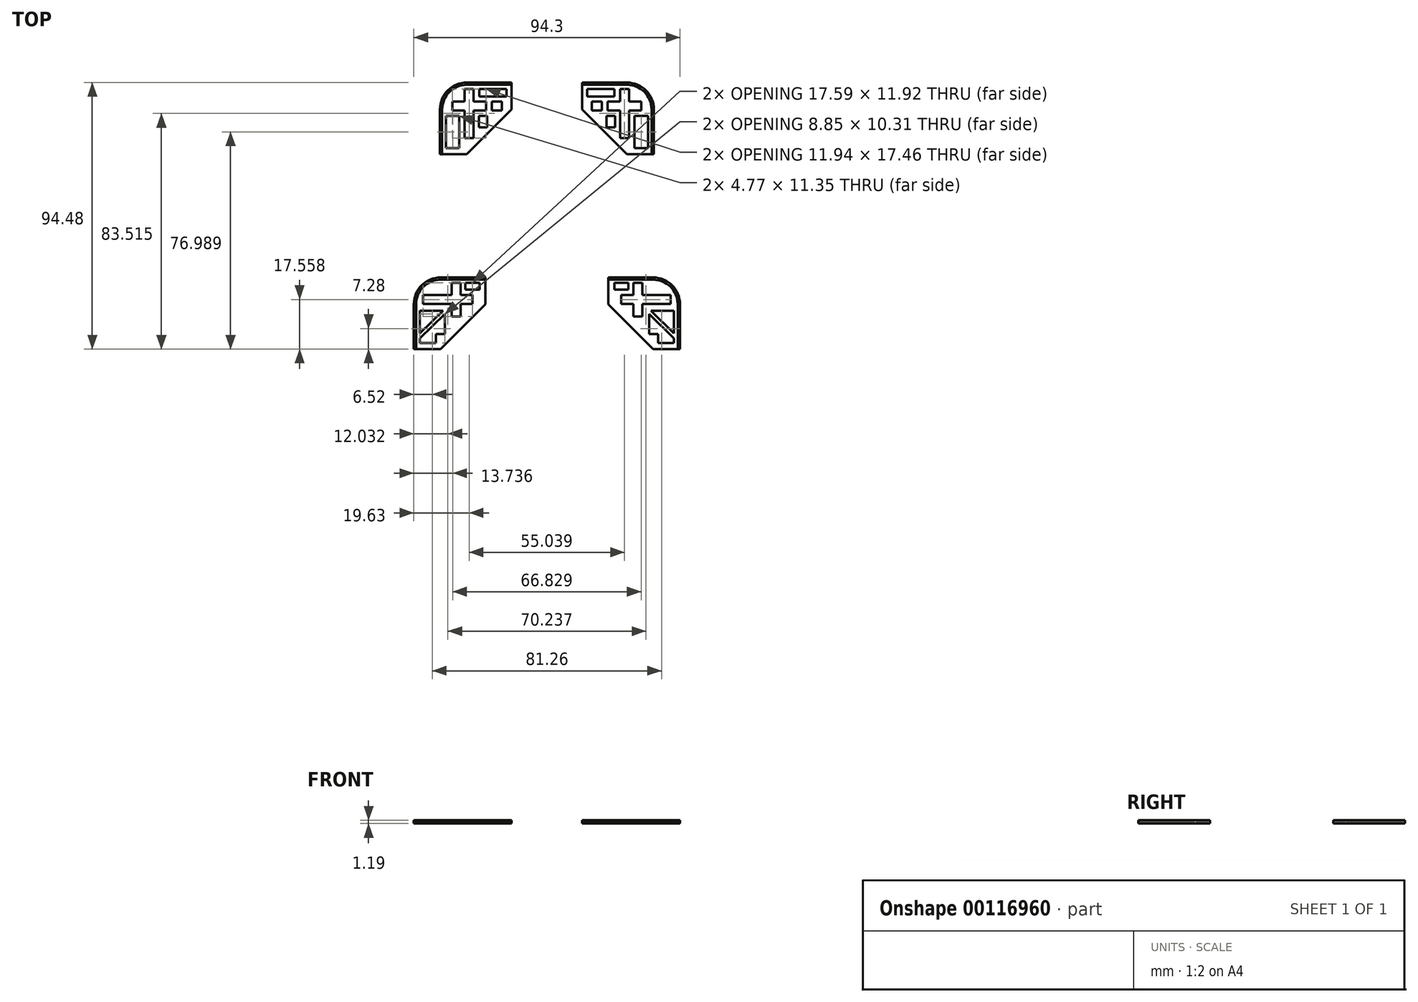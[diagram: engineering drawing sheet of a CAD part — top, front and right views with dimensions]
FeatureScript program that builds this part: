
annotation { "Feature Type Name" : "Feature", "Feature Type Description" : "" }
export const myFeature = defineFeature(function(context is Context, id is Id, definition is map)
    precondition{}
    {
        {
            var Q0;
            Q0=qCreatedBy(makeId("Top.planeOp"),FACE);
            var sketch = newSketch(context, id + "F0", { "sketchPlane" : qUnion([Q0])});
            skLineSegment(sketch, "E0", {"start": v(-37.9, 7.88) * mm, "end": v(-37.9, 23.75) * mm});
            skLineSegment(sketch, "E1", {"start": v(-37.9, 33.28) * mm, "end": v(-28.37, 33.28) * mm, "construction": true});
            skLineSegment(sketch, "E2", {"start": v(-37.9, 23.75) * mm, "end": v(-28.37, 23.75) * mm, "construction": true});
            skLineSegment(sketch, "E3", {"start": v(-28.37, 23.75) * mm, "end": v(-28.37, 33.28) * mm, "construction": true});
            skArc(sketch, "E4", {"start": v(-37.9, 23.75) * mm, "mid": v(-35.11, 30.49) * mm, "end": v(-28.37, 33.28) * mm});
            skLineSegment(sketch, "E5", {"start": v(-28.37, 33.28) * mm, "end": v(-12.5, 33.28) * mm});
            skLineSegment(sketch, "E6", {"start": v(-37.9, 23.75) * mm, "end": v(-37.9, 33.28) * mm, "construction": true});
            skLineSegment(sketch, "E7", {"start": v(-37.9, 7.88) * mm, "end": v(-28.37, 7.88) * mm});
            skLineSegment(sketch, "E8", {"start": v(-28.37, 7.88) * mm, "end": v(-12.5, 23.75) * mm});
            skLineSegment(sketch, "E9", {"start": v(-12.5, 23.75) * mm, "end": v(-12.5, 33.28) * mm});
            skLineSegment(sketch, "E10", {"start": v(-27.52, 35.55) * mm, "end": v(-27.52, 7.49) * mm, "construction": true});
            skLineSegment(sketch, "E11", {"start": v(-27.52, 31.05) * mm, "end": v(-29.1, 31.05) * mm});
            skLineSegment(sketch, "E12", {"start": v(-29.1, 31.05) * mm, "end": v(-29.1, 26.59) * mm});
            skLineSegment(sketch, "E13", {"start": v(-29.1, 26.59) * mm, "end": v(-33.5, 26.59) * mm});
            skLineSegment(sketch, "E14", {"start": v(-33.5, 26.59) * mm, "end": v(-33.5, 23.41) * mm});
            skLineSegment(sketch, "E15", {"start": v(-33.5, 23.41) * mm, "end": v(-29.1, 23.41) * mm});
            skLineSegment(sketch, "E16", {"start": v(-29.1, 23.41) * mm, "end": v(-29.1, 13.58) * mm});
            skLineSegment(sketch, "E17", {"start": v(-29.1, 13.58) * mm, "end": v(-27.52, 13.58) * mm});
            skLineSegment(sketch, "E18.MirrorCS", {"start": v(-27.52, 31.05) * mm, "end": v(-25.93, 31.05) * mm});
            skLineSegment(sketch, "E19.MirrorCS", {"start": v(-25.93, 31.05) * mm, "end": v(-25.93, 26.59) * mm});
            skLineSegment(sketch, "E20.MirrorCS", {"start": v(-25.93, 26.59) * mm, "end": v(-21.55, 26.59) * mm});
            skLineSegment(sketch, "E21.MirrorCS", {"start": v(-21.55, 26.59) * mm, "end": v(-21.55, 23.41) * mm});
            skLineSegment(sketch, "E22.MirrorCS", {"start": v(-21.55, 23.41) * mm, "end": v(-25.93, 23.41) * mm});
            skLineSegment(sketch, "E23.MirrorCS", {"start": v(-25.93, 23.41) * mm, "end": v(-25.93, 13.58) * mm});
            skLineSegment(sketch, "E24.MirrorCS", {"start": v(-25.93, 13.58) * mm, "end": v(-27.52, 13.58) * mm});
            skLineSegment(sketch, "E25.bottom", {"start": v(-23.9, 31.05) * mm, "end": v(-14.32, 31.05) * mm});
            skLineSegment(sketch, "E25.top", {"start": v(-23.9, 28.4) * mm, "end": v(-14.32, 28.4) * mm});
            skLineSegment(sketch, "E25.left", {"start": v(-23.9, 31.05) * mm, "end": v(-23.9, 28.4) * mm});
            skLineSegment(sketch, "E25.right", {"start": v(-14.32, 31.05) * mm, "end": v(-14.32, 28.4) * mm});
            skLineSegment(sketch, "E26.bottom", {"start": v(-24.13, 21.47) * mm, "end": v(-21.1, 21.47) * mm});
            skLineSegment(sketch, "E26.top", {"start": v(-24.13, 17.44) * mm, "end": v(-21.1, 17.44) * mm});
            skLineSegment(sketch, "E26.left", {"start": v(-24.13, 21.47) * mm, "end": v(-24.13, 17.44) * mm});
            skLineSegment(sketch, "E26.right", {"start": v(-21.1, 21.47) * mm, "end": v(-21.1, 17.44) * mm});
            skLineSegment(sketch, "E27.bottom", {"start": v(-31.03, 21.47) * mm, "end": v(-35.8, 21.47) * mm});
            skLineSegment(sketch, "E27.top", {"start": v(-31.03, 10.11) * mm, "end": v(-35.8, 10.11) * mm});
            skLineSegment(sketch, "E27.left", {"start": v(-31.03, 21.47) * mm, "end": v(-31.03, 10.11) * mm});
            skLineSegment(sketch, "E27.right", {"start": v(-35.8, 21.47) * mm, "end": v(-35.8, 10.11) * mm});
            skLineSegment(sketch, "E28.bottom", {"start": v(-19.47, 26.59) * mm, "end": v(-15.94, 26.59) * mm});
            skLineSegment(sketch, "E28.top", {"start": v(-19.47, 23.41) * mm, "end": v(-15.94, 23.41) * mm});
            skLineSegment(sketch, "E28.left", {"start": v(-19.47, 26.59) * mm, "end": v(-19.47, 23.41) * mm});
            skLineSegment(sketch, "E28.right", {"start": v(-15.94, 26.59) * mm, "end": v(-15.94, 23.41) * mm});
            skSolve(sketch);
        }
        {
            var Q0;
            Q0=makeQuery(id+"F0.imprint","IMPRINT",FACE,{"disambiguationData":[TD([[makeQuery(id+"F0.imprint","IMPRINT",EDGE,{"derivedFrom":sQuery(id+"F0.wireOp",EDGE,"E0")}),-1.0]])]});
            extrude(context, id + "F1", {"entities" : qUnion([Q0]), "depth" : 0.6 * mm});
        }
        {
            var Q0;
            Q0=makeQuery(id+"F1.opExtrude","SWEPT_BODY",BODY,{"disambiguationData":[OSD([sQuery(id+"F0.wireOp",EDGE,"E0"),sQuery(id+"F0.wireOp",EDGE,"E4"),sQuery(id+"F0.wireOp",EDGE,"E5"),sQuery(id+"F0.wireOp",EDGE,"E7"),sQuery(id+"F0.wireOp",EDGE,"E8"),sQuery(id+"F0.wireOp",EDGE,"E9"),sQuery(id+"F0.wireOp",EDGE,"E11"),sQuery(id+"F0.wireOp",EDGE,"E12"),sQuery(id+"F0.wireOp",EDGE,"E13"),sQuery(id+"F0.wireOp",EDGE,"E14"),sQuery(id+"F0.wireOp",EDGE,"E15"),sQuery(id+"F0.wireOp",EDGE,"E16"),sQuery(id+"F0.wireOp",EDGE,"E17"),sQuery(id+"F0.wireOp",EDGE,"E18.MirrorCS"),sQuery(id+"F0.wireOp",EDGE,"E19.MirrorCS"),sQuery(id+"F0.wireOp",EDGE,"E20.MirrorCS"),sQuery(id+"F0.wireOp",EDGE,"E21.MirrorCS"),sQuery(id+"F0.wireOp",EDGE,"E22.MirrorCS"),sQuery(id+"F0.wireOp",EDGE,"E23.MirrorCS"),sQuery(id+"F0.wireOp",EDGE,"E24.MirrorCS"),sQuery(id+"F0.wireOp",EDGE,"E25.bottom"),sQuery(id+"F0.wireOp",EDGE,"E25.top"),sQuery(id+"F0.wireOp",EDGE,"E25.left"),sQuery(id+"F0.wireOp",EDGE,"E25.right"),sQuery(id+"F0.wireOp",EDGE,"E26.bottom"),sQuery(id+"F0.wireOp",EDGE,"E26.top"),sQuery(id+"F0.wireOp",EDGE,"E26.left"),sQuery(id+"F0.wireOp",EDGE,"E26.right"),sQuery(id+"F0.wireOp",EDGE,"E27.bottom"),sQuery(id+"F0.wireOp",EDGE,"E27.top"),sQuery(id+"F0.wireOp",EDGE,"E27.left"),sQuery(id+"F0.wireOp",EDGE,"E27.right"),sQuery(id+"F0.wireOp",EDGE,"E28.bottom"),sQuery(id+"F0.wireOp",EDGE,"E28.top"),sQuery(id+"F0.wireOp",EDGE,"E28.left"),sQuery(id+"F0.wireOp",EDGE,"E28.right")])]});
            var Q1;
            Q1=qCreatedBy(makeId("Right.planeOp"),FACE);
            mirror(context, id + "F2", {"entities" : qUnion([Q0]), "mirrorPlane" : qUnion([Q1])});
        }
        {
            var Q0;
            Q0=qCreatedBy(makeId("Top.planeOp"),FACE);
            var sketch = newSketch(context, id + "F3", { "sketchPlane" : qUnion([Q0])});
            skLineSegment(sketch, "E29", {"start": v(-47.15, -61.2) * mm, "end": v(-47.15, -45.32) * mm});
            skLineSegment(sketch, "E30", {"start": v(-47.15, -35.8) * mm, "end": v(-37.63, -35.8) * mm, "construction": true});
            skLineSegment(sketch, "E31", {"start": v(-47.15, -45.32) * mm, "end": v(-37.63, -45.32) * mm, "construction": true});
            skLineSegment(sketch, "E32", {"start": v(-37.63, -45.32) * mm, "end": v(-37.63, -35.8) * mm, "construction": true});
            skArc(sketch, "E33", {"start": v(-47.15, -45.32) * mm, "mid": v(-44.36, -38.59) * mm, "end": v(-37.63, -35.8) * mm});
            skLineSegment(sketch, "E34", {"start": v(-37.63, -35.8) * mm, "end": v(-21.75, -35.8) * mm});
            skLineSegment(sketch, "E35", {"start": v(-47.15, -45.32) * mm, "end": v(-47.15, -35.8) * mm, "construction": true});
            skLineSegment(sketch, "E36", {"start": v(-47.15, -61.2) * mm, "end": v(-37.63, -61.2) * mm});
            skLineSegment(sketch, "E37", {"start": v(-37.63, -61.2) * mm, "end": v(-21.75, -45.32) * mm});
            skLineSegment(sketch, "E38", {"start": v(-21.75, -45.32) * mm, "end": v(-21.75, -35.8) * mm});
            skLineSegment(sketch, "E39.bottom", {"start": v(-36.85, -47.55) * mm, "end": v(-45.05, -47.55) * mm});
            skLineSegment(sketch, "E39.top", {"start": v(-36.2, -55.81) * mm, "end": v(-39.38, -55.81) * mm});
            skLineSegment(sketch, "E39.left", {"start": v(-36.2, -48.76) * mm, "end": v(-36.2, -55.81) * mm});
            skLineSegment(sketch, "E39.right", {"start": v(-45.05, -47.55) * mm, "end": v(-45.05, -55.57) * mm});
            skLineSegment(sketch, "E40", {"start": v(-26.32, -43.27) * mm, "end": v(-26.32, -42.05) * mm});
            skLineSegment(sketch, "E41", {"start": v(-26.32, -42.05) * mm, "end": v(-30.61, -42.05) * mm});
            skLineSegment(sketch, "E42", {"start": v(-30.61, -42.05) * mm, "end": v(-30.61, -37.68) * mm});
            skLineSegment(sketch, "E43", {"start": v(-30.61, -37.68) * mm, "end": v(-33.79, -37.68) * mm});
            skLineSegment(sketch, "E44", {"start": v(-33.79, -37.68) * mm, "end": v(-33.79, -42.05) * mm});
            skLineSegment(sketch, "E45", {"start": v(-33.79, -42.05) * mm, "end": v(-43.91, -42.05) * mm});
            skLineSegment(sketch, "E46", {"start": v(-43.91, -42.05) * mm, "end": v(-43.91, -45.23) * mm});
            skLineSegment(sketch, "E47", {"start": v(-43.91, -45.23) * mm, "end": v(-33.79, -45.23) * mm});
            skLineSegment(sketch, "E48", {"start": v(-33.79, -45.23) * mm, "end": v(-33.79, -49.6) * mm});
            skLineSegment(sketch, "E49", {"start": v(-33.79, -49.6) * mm, "end": v(-30.61, -49.6) * mm});
            skLineSegment(sketch, "E50", {"start": v(-30.61, -49.6) * mm, "end": v(-30.61, -45.23) * mm});
            skLineSegment(sketch, "E51", {"start": v(-30.61, -45.23) * mm, "end": v(-26.32, -45.23) * mm});
            skLineSegment(sketch, "E52", {"start": v(-26.32, -45.23) * mm, "end": v(-26.32, -43.27) * mm});
            skLineSegment(sketch, "E53.bottom", {"start": v(-28.87, -40.1) * mm, "end": v(-23.87, -40.1) * mm});
            skLineSegment(sketch, "E53.top", {"start": v(-28.87, -37.7) * mm, "end": v(-23.87, -37.7) * mm});
            skLineSegment(sketch, "E53.left", {"start": v(-28.87, -40.1) * mm, "end": v(-28.87, -37.7) * mm});
            skLineSegment(sketch, "E53.right", {"start": v(-23.87, -40.1) * mm, "end": v(-23.87, -37.7) * mm});
            skLineSegment(sketch, "E54.top", {"start": v(-45.05, -59.08) * mm, "end": v(-39.38, -59.08) * mm});
            skLineSegment(sketch, "E54.left", {"start": v(-45.05, -57.4) * mm, "end": v(-45.05, -59.08) * mm});
            skLineSegment(sketch, "E54.right", {"start": v(-39.38, -55.81) * mm, "end": v(-39.38, -59.08) * mm});
            skLineSegment(sketch, "E55", {"start": v(-36.85, -47.55) * mm, "end": v(-45.05, -55.57) * mm});
            skLineSegment(sketch, "E56", {"start": v(-36.2, -48.76) * mm, "end": v(-45.05, -57.4) * mm});
            skSolve(sketch);
        }
        {
            var Q0;
            Q0=makeQuery(id+"F3.imprint","IMPRINT",FACE,{"disambiguationData":[TD([[makeQuery(id+"F3.imprint","IMPRINT",EDGE,{"derivedFrom":sQuery(id+"F3.wireOp",EDGE,"E29")}),-1.0]])]});
            extrude(context, id + "F4", {"entities" : qUnion([Q0]), "depth" : 0.6 * mm});
        }
        {
            var Q0;
            Q0=makeQuery(id+"F4.opExtrude","SWEPT_BODY",BODY,{"disambiguationData":[OSD([sQuery(id+"F3.wireOp",EDGE,"E29"),sQuery(id+"F3.wireOp",EDGE,"E33"),sQuery(id+"F3.wireOp",EDGE,"E34"),sQuery(id+"F3.wireOp",EDGE,"E36"),sQuery(id+"F3.wireOp",EDGE,"E37"),sQuery(id+"F3.wireOp",EDGE,"E38"),sQuery(id+"F3.wireOp",EDGE,"E39.bottom"),sQuery(id+"F3.wireOp",EDGE,"E39.top"),sQuery(id+"F3.wireOp",EDGE,"E39.left"),sQuery(id+"F3.wireOp",EDGE,"E39.right"),sQuery(id+"F3.wireOp",EDGE,"E40"),sQuery(id+"F3.wireOp",EDGE,"E41"),sQuery(id+"F3.wireOp",EDGE,"E42"),sQuery(id+"F3.wireOp",EDGE,"E43"),sQuery(id+"F3.wireOp",EDGE,"E44"),sQuery(id+"F3.wireOp",EDGE,"E45"),sQuery(id+"F3.wireOp",EDGE,"E46"),sQuery(id+"F3.wireOp",EDGE,"E47"),sQuery(id+"F3.wireOp",EDGE,"E48"),sQuery(id+"F3.wireOp",EDGE,"E49"),sQuery(id+"F3.wireOp",EDGE,"E50"),sQuery(id+"F3.wireOp",EDGE,"E51"),sQuery(id+"F3.wireOp",EDGE,"E52"),sQuery(id+"F3.wireOp",EDGE,"E53.bottom"),sQuery(id+"F3.wireOp",EDGE,"E53.top"),sQuery(id+"F3.wireOp",EDGE,"E53.left"),sQuery(id+"F3.wireOp",EDGE,"E53.right"),sQuery(id+"F3.wireOp",EDGE,"E54.top"),sQuery(id+"F3.wireOp",EDGE,"E54.left"),sQuery(id+"F3.wireOp",EDGE,"E54.right"),sQuery(id+"F3.wireOp",EDGE,"E55"),sQuery(id+"F3.wireOp",EDGE,"E56")])]});
            var Q1;
            Q1=qCreatedBy(makeId("Right.planeOp"),FACE);
            mirror(context, id + "F5", {"entities" : qUnion([Q0]), "mirrorPlane" : qUnion([Q1])});
        }
        {
            var Q0;
            Q0=makeQuery(id+"F1.opExtrude","CAP_FACE",FACE,{"disambiguationData":[OSD([sQuery(id+"F0.wireOp",EDGE,"E0"),sQuery(id+"F0.wireOp",EDGE,"E4"),sQuery(id+"F0.wireOp",EDGE,"E5"),sQuery(id+"F0.wireOp",EDGE,"E7"),sQuery(id+"F0.wireOp",EDGE,"E8"),sQuery(id+"F0.wireOp",EDGE,"E9"),sQuery(id+"F0.wireOp",EDGE,"E11"),sQuery(id+"F0.wireOp",EDGE,"E12"),sQuery(id+"F0.wireOp",EDGE,"E13"),sQuery(id+"F0.wireOp",EDGE,"E14"),sQuery(id+"F0.wireOp",EDGE,"E15"),sQuery(id+"F0.wireOp",EDGE,"E16"),sQuery(id+"F0.wireOp",EDGE,"E17"),sQuery(id+"F0.wireOp",EDGE,"E18.MirrorCS"),sQuery(id+"F0.wireOp",EDGE,"E19.MirrorCS"),sQuery(id+"F0.wireOp",EDGE,"E20.MirrorCS"),sQuery(id+"F0.wireOp",EDGE,"E21.MirrorCS"),sQuery(id+"F0.wireOp",EDGE,"E22.MirrorCS"),sQuery(id+"F0.wireOp",EDGE,"E23.MirrorCS"),sQuery(id+"F0.wireOp",EDGE,"E24.MirrorCS"),sQuery(id+"F0.wireOp",EDGE,"E25.bottom"),sQuery(id+"F0.wireOp",EDGE,"E25.top"),sQuery(id+"F0.wireOp",EDGE,"E25.left"),sQuery(id+"F0.wireOp",EDGE,"E25.right"),sQuery(id+"F0.wireOp",EDGE,"E26.bottom"),sQuery(id+"F0.wireOp",EDGE,"E26.top"),sQuery(id+"F0.wireOp",EDGE,"E26.left"),sQuery(id+"F0.wireOp",EDGE,"E26.right"),sQuery(id+"F0.wireOp",EDGE,"E27.bottom"),sQuery(id+"F0.wireOp",EDGE,"E27.top"),sQuery(id+"F0.wireOp",EDGE,"E27.left"),sQuery(id+"F0.wireOp",EDGE,"E27.right"),sQuery(id+"F0.wireOp",EDGE,"E28.bottom"),sQuery(id+"F0.wireOp",EDGE,"E28.top"),sQuery(id+"F0.wireOp",EDGE,"E28.left"),sQuery(id+"F0.wireOp",EDGE,"E28.right")])],"isStart":false});
            var sketch = newSketch(context, id + "F6", { "sketchPlane" : qUnion([Q0])});
            skLineSegment(sketch, "E57.0", {"start": v(-28.37, 32.48) * mm, "end": v(-12.5, 32.48) * mm});
            skArc(sketch, "E57.1", {"start": v(-37.1, 23.75) * mm, "mid": v(-34.55, 29.93) * mm, "end": v(-28.37, 32.48) * mm});
            skLineSegment(sketch, "E57.2", {"start": v(-37.1, 7.88) * mm, "end": v(-37.1, 23.75) * mm});
            skArc(sketch, "E58.0", {"start": v(-37.9, 23.75) * mm, "mid": v(-35.11, 30.49) * mm, "end": v(-28.37, 33.28) * mm});
            skLineSegment(sketch, "E58.1", {"start": v(-28.37, 33.28) * mm, "end": v(-12.5, 33.28) * mm});
            skLineSegment(sketch, "E58.2", {"start": v(-37.9, 7.88) * mm, "end": v(-37.9, 23.75) * mm});
            skLineSegment(sketch, "E59", {"start": v(-12.5, 33.28) * mm, "end": v(-12.5, 32.48) * mm});
            skLineSegment(sketch, "E60", {"start": v(-37.9, 7.88) * mm, "end": v(-37.1, 7.88) * mm});
            skSolve(sketch);
        }
        {
            var Q0;
            Q0 = qSketchRegion(id + "F6", true);
            extrude(context, id + "F7", {"entities" : qUnion([Q0]), "operationType" : NewBodyOperationType.ADD, "depth" : 0.6 * mm});
        }
        {
            var Q0;
            Q0=makeQuery(id+"F1.opExtrude","SWEPT_BODY",BODY,{"disambiguationData":[OSD([sQuery(id+"F0.wireOp",EDGE,"E0"),sQuery(id+"F0.wireOp",EDGE,"E4"),sQuery(id+"F0.wireOp",EDGE,"E5"),sQuery(id+"F0.wireOp",EDGE,"E7"),sQuery(id+"F0.wireOp",EDGE,"E8"),sQuery(id+"F0.wireOp",EDGE,"E9"),sQuery(id+"F0.wireOp",EDGE,"E11"),sQuery(id+"F0.wireOp",EDGE,"E12"),sQuery(id+"F0.wireOp",EDGE,"E13"),sQuery(id+"F0.wireOp",EDGE,"E14"),sQuery(id+"F0.wireOp",EDGE,"E15"),sQuery(id+"F0.wireOp",EDGE,"E16"),sQuery(id+"F0.wireOp",EDGE,"E17"),sQuery(id+"F0.wireOp",EDGE,"E18.MirrorCS"),sQuery(id+"F0.wireOp",EDGE,"E19.MirrorCS"),sQuery(id+"F0.wireOp",EDGE,"E20.MirrorCS"),sQuery(id+"F0.wireOp",EDGE,"E21.MirrorCS"),sQuery(id+"F0.wireOp",EDGE,"E22.MirrorCS"),sQuery(id+"F0.wireOp",EDGE,"E23.MirrorCS"),sQuery(id+"F0.wireOp",EDGE,"E24.MirrorCS"),sQuery(id+"F0.wireOp",EDGE,"E25.bottom"),sQuery(id+"F0.wireOp",EDGE,"E25.top"),sQuery(id+"F0.wireOp",EDGE,"E25.left"),sQuery(id+"F0.wireOp",EDGE,"E25.right"),sQuery(id+"F0.wireOp",EDGE,"E26.bottom"),sQuery(id+"F0.wireOp",EDGE,"E26.top"),sQuery(id+"F0.wireOp",EDGE,"E26.left"),sQuery(id+"F0.wireOp",EDGE,"E26.right"),sQuery(id+"F0.wireOp",EDGE,"E27.bottom"),sQuery(id+"F0.wireOp",EDGE,"E27.top"),sQuery(id+"F0.wireOp",EDGE,"E27.left"),sQuery(id+"F0.wireOp",EDGE,"E27.right"),sQuery(id+"F0.wireOp",EDGE,"E28.bottom"),sQuery(id+"F0.wireOp",EDGE,"E28.top"),sQuery(id+"F0.wireOp",EDGE,"E28.left"),sQuery(id+"F0.wireOp",EDGE,"E28.right")])]});
            var Q1;
            Q1=qCreatedBy(makeId("Right.planeOp"),FACE);
            mirror(context, id + "F8", {"operationType" : NewBodyOperationType.ADD, "entities" : qUnion([Q0]), "mirrorPlane" : qUnion([Q1])});
        }
        {
            var Q0;
            Q0=makeQuery(id+"F4.opExtrude","CAP_FACE",FACE,{"disambiguationData":[OSD([sQuery(id+"F3.wireOp",EDGE,"E29"),sQuery(id+"F3.wireOp",EDGE,"E33"),sQuery(id+"F3.wireOp",EDGE,"E34"),sQuery(id+"F3.wireOp",EDGE,"E36"),sQuery(id+"F3.wireOp",EDGE,"E37"),sQuery(id+"F3.wireOp",EDGE,"E38"),sQuery(id+"F3.wireOp",EDGE,"E39.bottom"),sQuery(id+"F3.wireOp",EDGE,"E39.top"),sQuery(id+"F3.wireOp",EDGE,"E39.left"),sQuery(id+"F3.wireOp",EDGE,"E39.right"),sQuery(id+"F3.wireOp",EDGE,"E40"),sQuery(id+"F3.wireOp",EDGE,"E41"),sQuery(id+"F3.wireOp",EDGE,"E42"),sQuery(id+"F3.wireOp",EDGE,"E43"),sQuery(id+"F3.wireOp",EDGE,"E44"),sQuery(id+"F3.wireOp",EDGE,"E45"),sQuery(id+"F3.wireOp",EDGE,"E46"),sQuery(id+"F3.wireOp",EDGE,"E47"),sQuery(id+"F3.wireOp",EDGE,"E48"),sQuery(id+"F3.wireOp",EDGE,"E49"),sQuery(id+"F3.wireOp",EDGE,"E50"),sQuery(id+"F3.wireOp",EDGE,"E51"),sQuery(id+"F3.wireOp",EDGE,"E52"),sQuery(id+"F3.wireOp",EDGE,"E53.bottom"),sQuery(id+"F3.wireOp",EDGE,"E53.top"),sQuery(id+"F3.wireOp",EDGE,"E53.left"),sQuery(id+"F3.wireOp",EDGE,"E53.right"),sQuery(id+"F3.wireOp",EDGE,"E54.top"),sQuery(id+"F3.wireOp",EDGE,"E54.left"),sQuery(id+"F3.wireOp",EDGE,"E54.right"),sQuery(id+"F3.wireOp",EDGE,"E55"),sQuery(id+"F3.wireOp",EDGE,"E56")])],"isStart":false});
            var sketch = newSketch(context, id + "F9", { "sketchPlane" : qUnion([Q0])});
            skArc(sketch, "E61.0", {"start": v(-47.15, -45.32) * mm, "mid": v(-44.36, -38.59) * mm, "end": v(-37.63, -35.8) * mm});
            skLineSegment(sketch, "E61.1", {"start": v(-37.63, -35.8) * mm, "end": v(-21.75, -35.8) * mm});
            skLineSegment(sketch, "E61.2", {"start": v(-47.15, -61.2) * mm, "end": v(-47.15, -45.32) * mm});
            skLineSegment(sketch, "E62.0", {"start": v(-37.63, -36.6) * mm, "end": v(-21.75, -36.6) * mm});
            skArc(sketch, "E62.1", {"start": v(-46.36, -45.32) * mm, "mid": v(-43.8, -39.15) * mm, "end": v(-37.63, -36.6) * mm});
            skLineSegment(sketch, "E62.2", {"start": v(-46.36, -61.2) * mm, "end": v(-46.36, -45.32) * mm});
            skLineSegment(sketch, "E63", {"start": v(-21.75, -35.8) * mm, "end": v(-21.75, -36.6) * mm});
            skLineSegment(sketch, "E64", {"start": v(-46.36, -61.2) * mm, "end": v(-47.15, -61.2) * mm});
            skSolve(sketch);
        }
        {
            var Q0;
            Q0 = qSketchRegion(id + "F9", true);
            extrude(context, id + "F10", {"entities" : qUnion([Q0]), "operationType" : NewBodyOperationType.ADD, "depth" : 0.6 * mm});
        }
        {
            var Q0;
            Q0=makeQuery(id+"F4.opExtrude","SWEPT_BODY",BODY,{"disambiguationData":[OSD([sQuery(id+"F3.wireOp",EDGE,"E29"),sQuery(id+"F3.wireOp",EDGE,"E33"),sQuery(id+"F3.wireOp",EDGE,"E34"),sQuery(id+"F3.wireOp",EDGE,"E36"),sQuery(id+"F3.wireOp",EDGE,"E37"),sQuery(id+"F3.wireOp",EDGE,"E38"),sQuery(id+"F3.wireOp",EDGE,"E39.bottom"),sQuery(id+"F3.wireOp",EDGE,"E39.top"),sQuery(id+"F3.wireOp",EDGE,"E39.left"),sQuery(id+"F3.wireOp",EDGE,"E39.right"),sQuery(id+"F3.wireOp",EDGE,"E40"),sQuery(id+"F3.wireOp",EDGE,"E41"),sQuery(id+"F3.wireOp",EDGE,"E42"),sQuery(id+"F3.wireOp",EDGE,"E43"),sQuery(id+"F3.wireOp",EDGE,"E44"),sQuery(id+"F3.wireOp",EDGE,"E45"),sQuery(id+"F3.wireOp",EDGE,"E46"),sQuery(id+"F3.wireOp",EDGE,"E47"),sQuery(id+"F3.wireOp",EDGE,"E48"),sQuery(id+"F3.wireOp",EDGE,"E49"),sQuery(id+"F3.wireOp",EDGE,"E50"),sQuery(id+"F3.wireOp",EDGE,"E51"),sQuery(id+"F3.wireOp",EDGE,"E52"),sQuery(id+"F3.wireOp",EDGE,"E53.bottom"),sQuery(id+"F3.wireOp",EDGE,"E53.top"),sQuery(id+"F3.wireOp",EDGE,"E53.left"),sQuery(id+"F3.wireOp",EDGE,"E53.right"),sQuery(id+"F3.wireOp",EDGE,"E54.top"),sQuery(id+"F3.wireOp",EDGE,"E54.left"),sQuery(id+"F3.wireOp",EDGE,"E54.right"),sQuery(id+"F3.wireOp",EDGE,"E55"),sQuery(id+"F3.wireOp",EDGE,"E56")])]});
            var Q1;
            Q1=qCreatedBy(makeId("Right.planeOp"),FACE);
            mirror(context, id + "F11", {"operationType" : NewBodyOperationType.ADD, "entities" : qUnion([Q0]), "mirrorPlane" : qUnion([Q1])});
        }
    });
